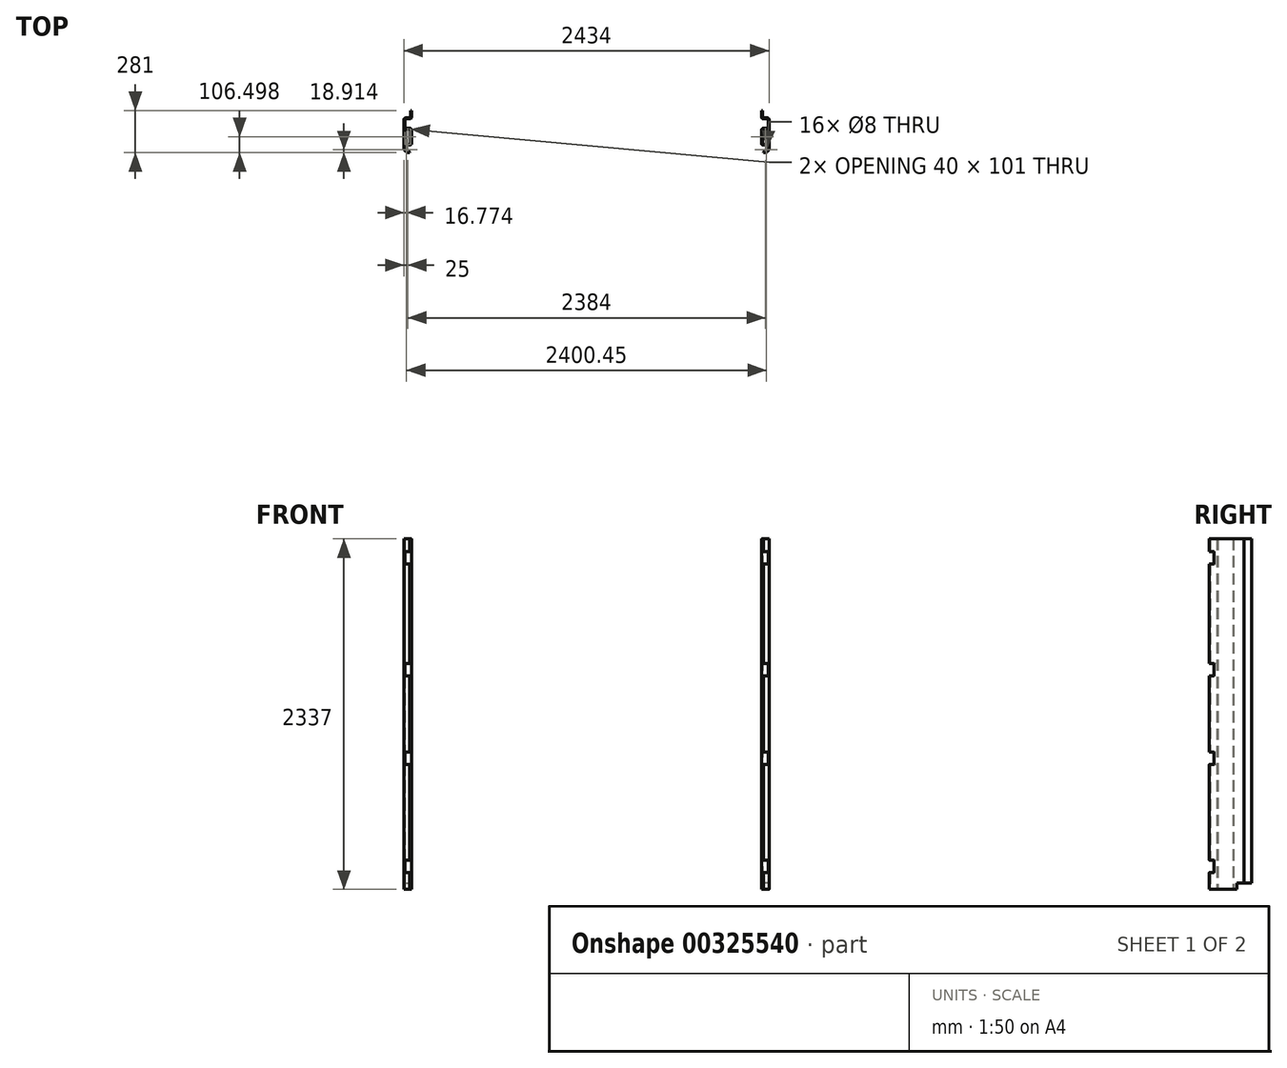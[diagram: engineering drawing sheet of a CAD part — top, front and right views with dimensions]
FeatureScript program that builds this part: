
annotation { "Feature Type Name" : "Feature", "Feature Type Description" : "" }
export const myFeature = defineFeature(function(context is Context, id is Id, definition is map)
    precondition{}
    {
        {
            var Q0;
            Q0=qCreatedBy(makeId("Top.planeOp"),FACE);
            var sketch = newSketch(context, id + "F0", { "sketchPlane" : qUnion([Q0])});
            skLineSegment(sketch, "E0", {"start": v(-45, 133.88) * mm, "end": v(-45, 88.88) * mm});
            skLineSegment(sketch, "E1", {"start": v(-45, 133.88) * mm, "end": v(-50, 133.88) * mm});
            skLineSegment(sketch, "E2", {"start": v(-50, 133.88) * mm, "end": v(-50, 88.88) * mm});
            skLineSegment(sketch, "E3", {"start": v(-40, 78.88) * mm, "end": v(-10, 78.88) * mm});
            skLineSegment(sketch, "E4", {"start": v(-5, 73.88) * mm, "end": v(-5, 19.88) * mm});
            skLineSegment(sketch, "E5", {"start": v(-10, 14.88) * mm, "end": v(-40, 14.88) * mm});
            skLineSegment(sketch, "E6", {"start": v(-50, 4.88) * mm, "end": v(-50, -86.12) * mm});
            skLineSegment(sketch, "E7", {"start": v(-40, -96.12) * mm, "end": v(-10, -96.12) * mm});
            skLineSegment(sketch, "E8", {"start": v(-5, -101.12) * mm, "end": v(-5, -112.12) * mm});
            skLineSegment(sketch, "E9", {"start": v(-35, -142.12) * mm, "end": v(-37, -142.12) * mm});
            skLineSegment(sketch, "E10", {"start": v(-37, -142.12) * mm, "end": v(-37, -147.12) * mm});
            skLineSegment(sketch, "E11", {"start": v(-37, -147.12) * mm, "end": v(-30, -147.12) * mm});
            skLineSegment(sketch, "E12", {"start": v(0, -117.12) * mm, "end": v(0, 73.88) * mm});
            skLineSegment(sketch, "E13", {"start": v(-10, 83.88) * mm, "end": v(-40, 83.88) * mm});
            skLineSegment(sketch, "E14", {"start": v(-40, 9.88) * mm, "end": v(-10, 9.88) * mm});
            skLineSegment(sketch, "E15", {"start": v(-45, 4.88) * mm, "end": v(-45, -86.12) * mm});
            skLineSegment(sketch, "E16", {"start": v(-40, -91.12) * mm, "end": v(-10, -91.12) * mm});
            skLineSegment(sketch, "E17", {"start": v(-5, 4.88) * mm, "end": v(-5, -86.12) * mm});
            skPoint(sketch, "E18.visualSharp", {"position": v(-5, -142.12) * mm});
            skArc(sketch, "E18.filletArc", {"start": v(-35, -142.12) * mm, "mid": v(-13.79, -133.34) * mm, "end": v(-5, -112.12) * mm});
            skPoint(sketch, "E19.visualSharp", {"position": v(0, -147.12) * mm});
            skArc(sketch, "E19.filletArc", {"start": v(-30, -147.12) * mm, "mid": v(-8.79, -138.34) * mm, "end": v(0, -117.12) * mm});
            skPoint(sketch, "E20.visualSharp", {"position": v(-45, 83.88) * mm});
            skArc(sketch, "E20.filletArc", {"start": v(-45, 88.88) * mm, "mid": v(-43.54, 85.34) * mm, "end": v(-40, 83.88) * mm});
            skPoint(sketch, "E21.visualSharp", {"position": v(-50, 78.88) * mm});
            skArc(sketch, "E21.filletArc", {"start": v(-50, 88.88) * mm, "mid": v(-47.07, 81.8) * mm, "end": v(-40, 78.88) * mm});
            skPoint(sketch, "E22.visualSharp", {"position": v(-5, 78.88) * mm});
            skArc(sketch, "E22.filletArc", {"start": v(-5, 73.88) * mm, "mid": v(-6.46, 77.41) * mm, "end": v(-10, 78.88) * mm});
            skPoint(sketch, "E23.visualSharp", {"position": v(0, 83.88) * mm});
            skArc(sketch, "E23.filletArc", {"start": v(0, 73.88) * mm, "mid": v(-2.93, 80.95) * mm, "end": v(-10, 83.88) * mm});
            skPoint(sketch, "E24.visualSharp", {"position": v(-45, 9.88) * mm});
            skArc(sketch, "E24.filletArc", {"start": v(-40, 9.88) * mm, "mid": v(-43.54, 8.41) * mm, "end": v(-45, 4.88) * mm});
            skPoint(sketch, "E25.visualSharp", {"position": v(-50, 14.88) * mm});
            skArc(sketch, "E25.filletArc", {"start": v(-40, 14.88) * mm, "mid": v(-47.07, 11.95) * mm, "end": v(-50, 4.88) * mm});
            skPoint(sketch, "E26.visualSharp", {"position": v(-5, 14.88) * mm});
            skArc(sketch, "E26.filletArc", {"start": v(-10, 14.88) * mm, "mid": v(-6.46, 16.34) * mm, "end": v(-5, 19.88) * mm});
            skPoint(sketch, "E27.visualSharp", {"position": v(-5, 9.88) * mm});
            skArc(sketch, "E27.filletArc", {"start": v(-5, 4.88) * mm, "mid": v(-6.46, 8.41) * mm, "end": v(-10, 9.88) * mm});
            skPoint(sketch, "E28.visualSharp", {"position": v(-45, -91.12) * mm});
            skArc(sketch, "E28.filletArc", {"start": v(-45, -86.12) * mm, "mid": v(-43.54, -89.66) * mm, "end": v(-40, -91.12) * mm});
            skPoint(sketch, "E29.visualSharp", {"position": v(-50, -96.12) * mm});
            skArc(sketch, "E29.filletArc", {"start": v(-50, -86.12) * mm, "mid": v(-47.07, -93.2) * mm, "end": v(-40, -96.12) * mm});
            skPoint(sketch, "E30.visualSharp", {"position": v(-5, -96.12) * mm});
            skArc(sketch, "E30.filletArc", {"start": v(-5, -101.12) * mm, "mid": v(-6.46, -97.59) * mm, "end": v(-10, -96.12) * mm});
            skPoint(sketch, "E31.visualSharp", {"position": v(-5, -91.12) * mm});
            skArc(sketch, "E31.filletArc", {"start": v(-10, -91.12) * mm, "mid": v(-6.46, -89.66) * mm, "end": v(-5, -86.12) * mm});
            skSolve(sketch);
        }
        {
            var Q0;
            Q0=makeQuery(id+"F0.imprint","IMPRINT",FACE,{"disambiguationData":[TD([[makeQuery(id+"F0.imprint","IMPRINT",EDGE,{"derivedFrom":sQuery(id+"F0.wireOp",EDGE,"E0")}),-1.0]])]});
            extrude(context, id + "F1", {"entities" : qUnion([Q0]), "offsetDistance" : 25 * mm, "depth" : 2337 * mm});
        }
        {
            var Q0;
            Q0=makeQuery(id+"F1.opExtrude","SWEPT_FACE",FACE,{"disambiguationData":[OSD([sQuery(id+"F0.wireOp",EDGE,"E12")])]});
            var sketch = newSketch(context, id + "F2", { "sketchPlane" : qUnion([Q0])});
            skLineSegment(sketch, "E32", {"start": v(36.79, 41) * mm, "end": v(135.95, 41) * mm});
            skLineSegment(sketch, "E33", {"start": v(135.95, 41) * mm, "end": v(135.95, -10.06) * mm});
            skLineSegment(sketch, "E34", {"start": v(135.95, -10.06) * mm, "end": v(36.79, -10.06) * mm});
            skLineSegment(sketch, "E35", {"start": v(-117.12, 2337) * mm, "end": v(-117.12, 2253) * mm});
            skLineSegment(sketch, "E36", {"start": v(-117.12, 2253) * mm, "end": v(-117.12, 2168) * mm});
            skLineSegment(sketch, "E37", {"start": v(-117.12, 2168) * mm, "end": v(-117.12, 1508) * mm});
            skLineSegment(sketch, "E38", {"start": v(-117.12, 1508) * mm, "end": v(-117.12, 1423) * mm});
            skLineSegment(sketch, "E39", {"start": v(-117.12, 1423) * mm, "end": v(-117.12, 916) * mm});
            skLineSegment(sketch, "E40", {"start": v(-117.12, 916) * mm, "end": v(-117.12, 831) * mm});
            skLineSegment(sketch, "E41", {"start": v(-117.12, 831) * mm, "end": v(-117.12, 196) * mm});
            skLineSegment(sketch, "E42", {"start": v(-117.12, 196) * mm, "end": v(-117.12, 111) * mm});
            skLineSegment(sketch, "E43", {"start": v(-117.12, 111) * mm, "end": v(-176.03, 111) * mm});
            skLineSegment(sketch, "E44", {"start": v(-176.03, 111) * mm, "end": v(-176.03, 196) * mm});
            skLineSegment(sketch, "E45", {"start": v(-176.03, 196) * mm, "end": v(-117.12, 196) * mm});
            skLineSegment(sketch, "E46", {"start": v(-117.12, 831) * mm, "end": v(-167.04, 831) * mm});
            skLineSegment(sketch, "E47", {"start": v(-117.12, 916) * mm, "end": v(-159.68, 916) * mm});
            skLineSegment(sketch, "E48", {"start": v(-159.68, 916) * mm, "end": v(-159.68, 831) * mm});
            skLineSegment(sketch, "E49", {"start": v(-117.12, 1508) * mm, "end": v(-157.23, 1508) * mm});
            skLineSegment(sketch, "E50", {"start": v(-157.23, 1508) * mm, "end": v(-157.23, 1423) * mm});
            skLineSegment(sketch, "E51", {"start": v(-157.23, 1423) * mm, "end": v(-117.12, 1423) * mm});
            skLineSegment(sketch, "E52", {"start": v(-117.12, 2253) * mm, "end": v(-157.23, 2253) * mm});
            skLineSegment(sketch, "E53", {"start": v(-157.23, 2253) * mm, "end": v(-157.23, 2168) * mm});
            skLineSegment(sketch, "E54", {"start": v(-157.23, 2168) * mm, "end": v(-117.12, 2168) * mm});
            skLineSegment(sketch, "E55", {"start": v(36.79, 41) * mm, "end": v(36.79, -10.06) * mm});
            skSolve(sketch);
        }
        {
            var Q0;
            {var subQ1=sQuery(id+"F2.wireOp",EDGE,"E33");Q0=makeQuery(id+"F2.imprint","IMPRINT",FACE,{"disambiguationData":[TD([[makeQuery(id+"F2.imprint","IMPRINT",EDGE,{"derivedFrom":subQ1}),-1.0]])]});}
            var Q1;
            {var subQ0=sQuery(id+"F2.wireOp",EDGE,"rInhrVmb-6rYZ-AbAy-IgbS-Yb71Ue1Th2yZ");Q1=makeQuery(id+"F2.imprint","IMPRINT",FACE,{"disambiguationData":[TD([[makeQuery(id+"F2.imprint","IMPRINT",EDGE,{"derivedFrom":subQ0}),-1.0]])]});}
            var Q2;
            Q2=makeQuery(id+"F2.imprint","IMPRINT",FACE,{"disambiguationData":[TD([[makeQuery(id+"F2.imprint","IMPRINT",EDGE,{"derivedFrom":sQuery(id+"F2.wireOp",EDGE,"E42")}),-1.0]])]});
            var Q3;
            {var subQ0=sQuery(id+"F2.wireOp",EDGE,"E40");Q3=makeQuery(id+"F2.imprint","IMPRINT",FACE,{"disambiguationData":[TD([[makeQuery(id+"F2.imprint","IMPRINT",EDGE,{"derivedFrom":subQ0}),-1.0]])]});}
            var Q4;
            Q4=makeQuery(id+"F2.imprint","IMPRINT",FACE,{"disambiguationData":[TD([[makeQuery(id+"F2.imprint","IMPRINT",EDGE,{"derivedFrom":sQuery(id+"F2.wireOp",EDGE,"E38")}),-1.0]])]});
            var Q5;
            Q5=makeQuery(id+"F2.imprint","IMPRINT",FACE,{"disambiguationData":[TD([[makeQuery(id+"F2.imprint","IMPRINT",EDGE,{"derivedFrom":sQuery(id+"F2.wireOp",EDGE,"E36")}),-1.0]])]});
            var Q6;
            {var subQ0=sQuery(id+"F2.wireOp",EDGE,"E55");var subQ1=sQuery(id+"F2.wireOp",EDGE,"E32");var subQ2=makeQuery(id+"F2.imprint","INTERSECT",VERTEX,{"derivedFrom":[subQ1,subQ0]});Q6=makeQuery(id+"F2.imprint","IMPRINT",FACE,{"disambiguationData":[TD([[makeQuery(id+"F2.imprint","IMPRINT",EDGE,{"disambiguationData":[TD([[subQ2,-1.0]])],"derivedFrom":subQ0}),1.0]])]});}
            extrude(context, id + "F3", {"entities" : qUnion([Q0, Q1, Q2, Q3, Q4, Q5, Q6]), "operationType" : NewBodyOperationType.REMOVE, "oppositeDirection" : true, "depth" : 55 * mm});
        }
        {
            var Q0;
            Q0=makeQuery(id+"F3.boolean.opBoolean","COPY",FACE,{"derivedFrom":makeQuery(id+"F3.opExtrude","SWEPT_FACE",FACE,{"disambiguationData":[OSD([sQuery(id+"F2.wireOp",EDGE,"E52")])]})});
            var sketch = newSketch(context, id + "F4", { "sketchPlane" : qUnion([Q0])});
            skLineSegment(sketch, "E56", {"start": v(-37, 147.12) * mm, "end": v(-37, 142.12) * mm});
            skLineSegment(sketch, "E57", {"start": v(-37, 142.12) * mm, "end": v(0, 101.12) * mm});
            skLineSegment(sketch, "E58", {"start": v(0, 101.12) * mm, "end": v(0, 117.12) * mm});
            skLineSegment(sketch, "E59", {"start": v(-37, 147.12) * mm, "end": v(-30, 147.12) * mm});
            skSolve(sketch);
        }
        {
            var Q0;
            Q0=makeQuery(id+"F4.imprint","IMPRINT",FACE,{"disambiguationData":[TD([[makeQuery(id+"F4.imprint","IMPRINT",EDGE,{"derivedFrom":sQuery(id+"F4.wireOp",EDGE,"E57")}),1.0]])]});
            var Q1;
            Q1=makeQuery(id+"F4.imprint","IMPRINT",FACE,{"disambiguationData":[TD([[makeQuery(id+"F4.imprint","IMPRINT",EDGE,{"derivedFrom":sQuery(id+"F4.wireOp",EDGE,"E56")}),-1.0]])]});
            extrude(context, id + "F5", {"entities" : qUnion([Q0, Q1]), "operationType" : NewBodyOperationType.ADD, "depth" : 2 * mm});
        }
        {
            var Q0;
            Q0=makeQuery(id+"F3.boolean.opBoolean","COPY",FACE,{"derivedFrom":makeQuery(id+"F3.opExtrude","SWEPT_FACE",FACE,{"disambiguationData":[OSD([sQuery(id+"F2.wireOp",EDGE,"E54")])]})});
            var sketch = newSketch(context, id + "F6", { "sketchPlane" : qUnion([Q0])});
            skLineSegment(sketch, "E60", {"start": v(-37, -147.12) * mm, "end": v(-37, -142.12) * mm});
            skLineSegment(sketch, "E61", {"start": v(-37, -142.12) * mm, "end": v(0, -101.12) * mm});
            skLineSegment(sketch, "E62", {"start": v(0, -101.12) * mm, "end": v(0, -117.12) * mm});
            skSolve(sketch);
        }
        {
            var Q0;
            Q0=makeQuery(id+"F6.imprint","IMPRINT",FACE,{"disambiguationData":[TD([[makeQuery(id+"F6.imprint","IMPRINT",EDGE,{"derivedFrom":sQuery(id+"F6.wireOp",EDGE,"E61")}),-1.0]])]});
            var Q1;
            Q1=makeQuery(id+"F6.imprint","IMPRINT",FACE,{"disambiguationData":[TD([[makeQuery(id+"F6.imprint","IMPRINT",EDGE,{"derivedFrom":sQuery(id+"F6.wireOp",EDGE,"E60")}),-1.0]])]});
            extrude(context, id + "F7", {"entities" : qUnion([Q0, Q1]), "operationType" : NewBodyOperationType.ADD, "depth" : 2 * mm});
        }
        {
            var Q0;
            Q0=makeQuery(id+"F3.boolean.opBoolean","COPY",FACE,{"derivedFrom":makeQuery(id+"F3.opExtrude","SWEPT_FACE",FACE,{"disambiguationData":[OSD([sQuery(id+"F2.wireOp",EDGE,"E49")])]})});
            var sketch = newSketch(context, id + "F8", { "sketchPlane" : qUnion([Q0])});
            skLineSegment(sketch, "E63", {"start": v(-37, 147.12) * mm, "end": v(-37, 142.12) * mm});
            skLineSegment(sketch, "E64", {"start": v(-37, 142.12) * mm, "end": v(0, 101.12) * mm});
            skLineSegment(sketch, "E65", {"start": v(0, 101.12) * mm, "end": v(0, 117.12) * mm});
            skLineSegment(sketch, "E66", {"start": v(-37, 147.12) * mm, "end": v(-30, 147.12) * mm});
            skSolve(sketch);
        }
        {
            var Q0;
            Q0=makeQuery(id+"F8.imprint","IMPRINT",FACE,{"disambiguationData":[TD([[makeQuery(id+"F8.imprint","IMPRINT",EDGE,{"derivedFrom":sQuery(id+"F8.wireOp",EDGE,"E64")}),1.0]])]});
            var Q1;
            Q1=makeQuery(id+"F8.imprint","IMPRINT",FACE,{"disambiguationData":[TD([[makeQuery(id+"F8.imprint","IMPRINT",EDGE,{"derivedFrom":sQuery(id+"F8.wireOp",EDGE,"E63")}),-1.0]])]});
            extrude(context, id + "F9", {"entities" : qUnion([Q0, Q1]), "operationType" : NewBodyOperationType.ADD, "depth" : 2 * mm});
        }
        {
            var Q0;
            Q0=makeQuery(id+"F3.boolean.opBoolean","COPY",FACE,{"derivedFrom":makeQuery(id+"F3.opExtrude","SWEPT_FACE",FACE,{"disambiguationData":[OSD([sQuery(id+"F2.wireOp",EDGE,"E51")])]})});
            var sketch = newSketch(context, id + "F10", { "sketchPlane" : qUnion([Q0])});
            skLineSegment(sketch, "E67", {"start": v(-37, -142.12) * mm, "end": v(-37, -147.12) * mm});
            skLineSegment(sketch, "E68", {"start": v(-37, -147.12) * mm, "end": v(-30, -147.12) * mm});
            skLineSegment(sketch, "E69", {"start": v(0, -117.12) * mm, "end": v(0, -101.12) * mm});
            skLineSegment(sketch, "E70", {"start": v(0, -101.12) * mm, "end": v(-37, -142.12) * mm});
            skSolve(sketch);
        }
        {
            var Q0;
            Q0 = qSketchRegion(id + "F10", true);
            var Q1;
            Q1=makeQuery(id+"F10.imprint","IMPRINT",FACE,{"disambiguationData":[TD([[makeQuery(id+"F10.imprint","IMPRINT",EDGE,{"derivedFrom":sQuery(id+"F10.wireOp",EDGE,"E67")}),-1.0]])]});
            var Q2;
            Q2=makeQuery(id+"F10.imprint","IMPRINT",FACE,{"disambiguationData":[TD([[makeQuery(id+"F10.imprint","IMPRINT",EDGE,{"derivedFrom":sQuery(id+"F10.wireOp",EDGE,"E69")}),1.0]])]});
            extrude(context, id + "F11", {"entities" : qUnion([Q0, Q1, Q2]), "operationType" : NewBodyOperationType.ADD, "depth" : 2 * mm});
        }
        {
            var Q0;
            Q0=makeQuery(id+"F3.boolean.opBoolean","COPY",FACE,{"derivedFrom":makeQuery(id+"F3.opExtrude","SWEPT_FACE",FACE,{"disambiguationData":[OSD([sQuery(id+"F2.wireOp",EDGE,"E47")])]})});
            var sketch = newSketch(context, id + "F12", { "sketchPlane" : qUnion([Q0])});
            skLineSegment(sketch, "E71", {"start": v(-37, 142.12) * mm, "end": v(-37, 147.12) * mm});
            skLineSegment(sketch, "E72", {"start": v(-37, 147.12) * mm, "end": v(-30, 147.12) * mm});
            skLineSegment(sketch, "E73", {"start": v(0, 117.12) * mm, "end": v(0, 101.12) * mm});
            skLineSegment(sketch, "E74", {"start": v(0, 101.12) * mm, "end": v(-37, 142.12) * mm});
            skSolve(sketch);
        }
        {
            var Q0;
            Q0=makeQuery(id+"F12.imprint","IMPRINT",FACE,{"disambiguationData":[TD([[makeQuery(id+"F12.imprint","IMPRINT",EDGE,{"derivedFrom":sQuery(id+"F12.wireOp",EDGE,"E73")}),-1.0]])]});
            var Q1;
            Q1=makeQuery(id+"F12.imprint","IMPRINT",FACE,{"disambiguationData":[TD([[makeQuery(id+"F12.imprint","IMPRINT",EDGE,{"derivedFrom":sQuery(id+"F12.wireOp",EDGE,"E71")}),-1.0]])]});
            extrude(context, id + "F13", {"entities" : qUnion([Q0, Q1]), "operationType" : NewBodyOperationType.ADD, "depth" : 2 * mm});
        }
        {
            var Q0;
            Q0=makeQuery(id+"F3.boolean.opBoolean","COPY",FACE,{"derivedFrom":makeQuery(id+"F3.opExtrude","SWEPT_FACE",FACE,{"disambiguationData":[OSD([sQuery(id+"F2.wireOp",EDGE,"E46")])]})});
            var sketch = newSketch(context, id + "F14", { "sketchPlane" : qUnion([Q0])});
            skLineSegment(sketch, "E75", {"start": v(-37, -142.12) * mm, "end": v(-37, -147.12) * mm});
            skLineSegment(sketch, "E76", {"start": v(-37, -147.12) * mm, "end": v(-30, -147.12) * mm});
            skLineSegment(sketch, "E77", {"start": v(0, -117.12) * mm, "end": v(0, -101.12) * mm});
            skLineSegment(sketch, "E78", {"start": v(0, -101.12) * mm, "end": v(-37, -142.12) * mm});
            skSolve(sketch);
        }
        {
            var Q0;
            Q0=makeQuery(id+"F14.imprint","IMPRINT",FACE,{"disambiguationData":[TD([[makeQuery(id+"F14.imprint","IMPRINT",EDGE,{"derivedFrom":sQuery(id+"F14.wireOp",EDGE,"E77")}),1.0]])]});
            var Q1;
            Q1=makeQuery(id+"F14.imprint","IMPRINT",FACE,{"disambiguationData":[TD([[makeQuery(id+"F14.imprint","IMPRINT",EDGE,{"derivedFrom":sQuery(id+"F14.wireOp",EDGE,"E75")}),1.0]])]});
            extrude(context, id + "F15", {"entities" : qUnion([Q0, Q1]), "operationType" : NewBodyOperationType.ADD, "depth" : 2 * mm});
        }
        {
            var Q0;
            Q0=makeQuery(id+"F3.boolean.opBoolean","COPY",FACE,{"derivedFrom":makeQuery(id+"F3.opExtrude","SWEPT_FACE",FACE,{"disambiguationData":[OSD([sQuery(id+"F2.wireOp",EDGE,"E45")])]})});
            var sketch = newSketch(context, id + "F16", { "sketchPlane" : qUnion([Q0])});
            skLineSegment(sketch, "E79", {"start": v(-37, 142.12) * mm, "end": v(-37, 147.12) * mm});
            skLineSegment(sketch, "E80", {"start": v(-37, 147.12) * mm, "end": v(-30, 147.12) * mm});
            skLineSegment(sketch, "E81", {"start": v(0, 117.12) * mm, "end": v(0, 101.12) * mm});
            skLineSegment(sketch, "E82", {"start": v(0, 101.12) * mm, "end": v(-37, 142.12) * mm});
            skSolve(sketch);
        }
        {
            var Q0;
            Q0=makeQuery(id+"F16.imprint","IMPRINT",FACE,{"disambiguationData":[TD([[makeQuery(id+"F16.imprint","IMPRINT",EDGE,{"derivedFrom":sQuery(id+"F16.wireOp",EDGE,"E81")}),-1.0]])]});
            var Q1;
            Q1=makeQuery(id+"F16.imprint","IMPRINT",FACE,{"disambiguationData":[TD([[makeQuery(id+"F16.imprint","IMPRINT",EDGE,{"derivedFrom":sQuery(id+"F16.wireOp",EDGE,"E79")}),1.0]])]});
            extrude(context, id + "F17", {"entities" : qUnion([Q0, Q1]), "operationType" : NewBodyOperationType.ADD, "depth" : 2 * mm});
        }
        {
            var Q0;
            Q0=makeQuery(id+"F3.boolean.opBoolean","COPY",FACE,{"derivedFrom":makeQuery(id+"F3.opExtrude","SWEPT_FACE",FACE,{"disambiguationData":[OSD([sQuery(id+"F2.wireOp",EDGE,"E43")])]})});
            var sketch = newSketch(context, id + "F18", { "sketchPlane" : qUnion([Q0])});
            skLineSegment(sketch, "E83", {"start": v(-37, -142.12) * mm, "end": v(-37, -147.12) * mm});
            skLineSegment(sketch, "E84", {"start": v(-37, -147.12) * mm, "end": v(-30, -147.12) * mm});
            skLineSegment(sketch, "E85", {"start": v(0, -117.12) * mm, "end": v(0, -101.12) * mm});
            skLineSegment(sketch, "E86", {"start": v(0, -101.12) * mm, "end": v(-37, -142.12) * mm});
            skSolve(sketch);
        }
        {
            var Q0;
            Q0=makeQuery(id+"F18.imprint","IMPRINT",FACE,{"disambiguationData":[TD([[makeQuery(id+"F18.imprint","IMPRINT",EDGE,{"derivedFrom":sQuery(id+"F18.wireOp",EDGE,"E85")}),1.0]])]});
            var Q1;
            Q1=makeQuery(id+"F18.imprint","IMPRINT",FACE,{"disambiguationData":[TD([[makeQuery(id+"F18.imprint","IMPRINT",EDGE,{"derivedFrom":sQuery(id+"F18.wireOp",EDGE,"E83")}),1.0]])]});
            extrude(context, id + "F19", {"entities" : qUnion([Q0, Q1]), "operationType" : NewBodyOperationType.ADD, "depth" : 2 * mm});
        }
        {
            var Q0;
            Q0=makeQuery(id+"F19.opExtrude","CAP_FACE",FACE,{"disambiguationData":[OSD([sQuery(id+"F0.wireOp",EDGE,"E19.filletArc"),sQuery(id+"F2.wireOp",EDGE,"E43"),sQuery(id+"F18.wireOp",EDGE,"E83"),sQuery(id+"F18.wireOp",EDGE,"E84"),sQuery(id+"F18.wireOp",EDGE,"E85"),sQuery(id+"F18.wireOp",EDGE,"E86")])],"isStart":true});
            var sketch = newSketch(context, id + "F20", { "sketchPlane" : qUnion([Q0])});
            skLineSegment(sketch, "E87", {"start": v(-21, 124.4) * mm, "end": v(-12.55, 132.02) * mm});
            skCircle(sketch, "E88", {"center": v(-16.77, 128.2) * mm, "radius": 4 * mm});
            skSolve(sketch);
        }
        {
            var Q0;
            {var subQ0=sQuery(id+"F20.wireOp",EDGE,"E88");var subQ1=sQuery(id+"F20.wireOp",EDGE,"E87");var subQ2=makeQuery(id+"F20.imprint","INTERSECT",VERTEX,{"disambiguationData":[OD(0.0)],"derivedFrom":[subQ1,subQ0]});Q0=makeQuery(id+"F20.imprint","IMPRINT",FACE,{"disambiguationData":[TD([[makeQuery(id+"F20.imprint","IMPRINT",EDGE,{"disambiguationData":[TD([[subQ2,-1.0]])],"derivedFrom":subQ1}),1.0]])]});}
            var Q1;
            {var subQ0=sQuery(id+"F20.wireOp",EDGE,"E88");var subQ1=sQuery(id+"F20.wireOp",EDGE,"E87");var subQ2=makeQuery(id+"F20.imprint","INTERSECT",VERTEX,{"disambiguationData":[OD(0.0)],"derivedFrom":[subQ1,subQ0]});Q1=makeQuery(id+"F20.imprint","IMPRINT",FACE,{"disambiguationData":[TD([[makeQuery(id+"F20.imprint","IMPRINT",EDGE,{"disambiguationData":[TD([[subQ2,-1.0]])],"derivedFrom":subQ1}),-1.0]])]});}
            extrude(context, id + "F21", {"entities" : qUnion([Q0, Q1]), "operationType" : NewBodyOperationType.REMOVE, "oppositeDirection" : true, "depth" : 2337 * mm});
        }
        {
            var Q0;
            Q0=makeQuery(id+"F1.opExtrude","SWEPT_FACE",FACE,{"disambiguationData":[OSD([sQuery(id+"F0.wireOp",EDGE,"E6")])]});
            cPlane(context, id + "F22", {"entities" : qUnion([Q0]), "cplaneType" : CPlaneType.OFFSET, "offset" : 1167 * mm, "width" : 150 * mm, "height" : 150 * mm});
        }
        {
            var Q0;
            Q0=makeQuery(id+"F1.opExtrude","SWEPT_BODY",BODY,{"disambiguationData":[OSD([sQuery(id+"F0.wireOp",EDGE,"E0"),sQuery(id+"F0.wireOp",EDGE,"E1"),sQuery(id+"F0.wireOp",EDGE,"E2"),sQuery(id+"F0.wireOp",EDGE,"E3"),sQuery(id+"F0.wireOp",EDGE,"E4"),sQuery(id+"F0.wireOp",EDGE,"E5"),sQuery(id+"F0.wireOp",EDGE,"E6"),sQuery(id+"F0.wireOp",EDGE,"E7"),sQuery(id+"F0.wireOp",EDGE,"E8"),sQuery(id+"F0.wireOp",EDGE,"E9"),sQuery(id+"F0.wireOp",EDGE,"E10"),sQuery(id+"F0.wireOp",EDGE,"E11"),sQuery(id+"F0.wireOp",EDGE,"E12"),sQuery(id+"F0.wireOp",EDGE,"E13"),sQuery(id+"F0.wireOp",EDGE,"E14"),sQuery(id+"F0.wireOp",EDGE,"E15"),sQuery(id+"F0.wireOp",EDGE,"E16"),sQuery(id+"F0.wireOp",EDGE,"E17"),sQuery(id+"F0.wireOp",EDGE,"E18.filletArc"),sQuery(id+"F0.wireOp",EDGE,"E19.filletArc"),sQuery(id+"F0.wireOp",EDGE,"E20.filletArc"),sQuery(id+"F0.wireOp",EDGE,"E21.filletArc"),sQuery(id+"F0.wireOp",EDGE,"E22.filletArc"),sQuery(id+"F0.wireOp",EDGE,"E23.filletArc"),sQuery(id+"F0.wireOp",EDGE,"E24.filletArc"),sQuery(id+"F0.wireOp",EDGE,"E25.filletArc"),sQuery(id+"F0.wireOp",EDGE,"E26.filletArc"),sQuery(id+"F0.wireOp",EDGE,"E27.filletArc"),sQuery(id+"F0.wireOp",EDGE,"E28.filletArc"),sQuery(id+"F0.wireOp",EDGE,"E29.filletArc"),sQuery(id+"F0.wireOp",EDGE,"E30.filletArc"),sQuery(id+"F0.wireOp",EDGE,"E31.filletArc")])]});
            var Q1;
            Q1=qCreatedBy(id+"F22.planeOp",FACE);
            mirror(context, id + "F23", {"entities" : qUnion([Q0]), "mirrorPlane" : qUnion([Q1])});
        }
    });
